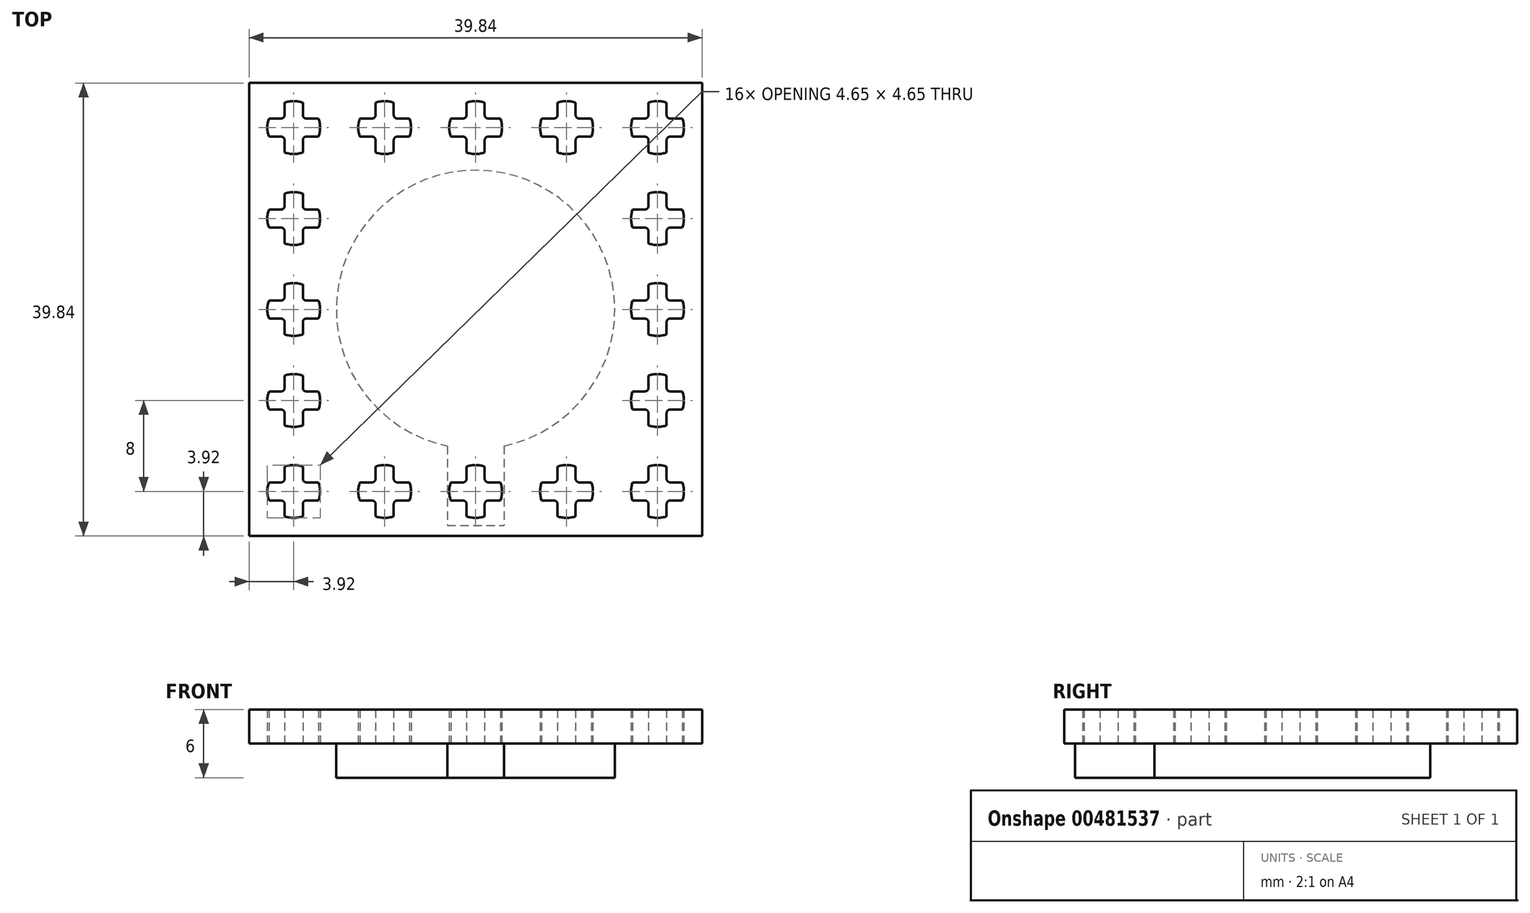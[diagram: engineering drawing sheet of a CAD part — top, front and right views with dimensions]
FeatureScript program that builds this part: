
annotation { "Feature Type Name" : "Feature", "Feature Type Description" : "" }
export const myFeature = defineFeature(function(context is Context, id is Id, definition is map)
    precondition{}
    {
        {
            var Q0;
            Q0=qCreatedBy(makeId("Top.planeOp"),FACE);
            var sketch = newSketch(context, id + "F0", { "sketchPlane" : qUnion([Q0])});
            skLineSegment(sketch, "E0.bottom", {"start": v(-20, 20) * mm, "end": v(20, 20) * mm});
            skLineSegment(sketch, "E0.top", {"start": v(-20, -20) * mm, "end": v(20, -20) * mm});
            skLineSegment(sketch, "E0.left", {"start": v(-20, 20) * mm, "end": v(-20, -20) * mm});
            skLineSegment(sketch, "E0.right", {"start": v(20, 20) * mm, "end": v(20, -20) * mm});
            skLineSegment(sketch, "E1", {"start": v(-16.8, 18.18) * mm, "end": v(-15.2, 18.18) * mm, "construction": true});
            skLineSegment(sketch, "E2", {"start": v(-15.2, 18.18) * mm, "end": v(-15.2, 17.1) * mm});
            skLineSegment(sketch, "E3", {"start": v(-14.9, 16.8) * mm, "end": v(-13.82, 16.8) * mm});
            skLineSegment(sketch, "E4", {"start": v(-13.82, 16.8) * mm, "end": v(-16, 16) * mm, "construction": true});
            skLineSegment(sketch, "E5", {"start": v(-16, 16) * mm, "end": v(-16.8, 18.18) * mm, "construction": true});
            skArc(sketch, "E6", {"start": v(-15.2, 18.18) * mm, "mid": v(-16, 18.32) * mm, "end": v(-16.8, 18.18) * mm});
            skArc(sketch, "E7", {"start": v(-15.2, 17.1) * mm, "mid": v(-15.11, 16.89) * mm, "end": v(-14.9, 16.8) * mm});
            skLineSegment(sketch, "E8", {"start": v(-15.2, 18.18) * mm, "end": v(-15.2, 16.8) * mm, "construction": true});
            skLineSegment(sketch, "E9", {"start": v(-15.2, 16.8) * mm, "end": v(-13.82, 16.8) * mm, "construction": true});
            skArc(sketch, "E10.1.0", {"start": v(-18.18, 16.8) * mm, "mid": v(-18.32, 16) * mm, "end": v(-18.18, 15.2) * mm});
            skArc(sketch, "E10.1.1", {"start": v(-17.1, 16.8) * mm, "mid": v(-16.89, 16.89) * mm, "end": v(-16.8, 17.1) * mm});
            skLineSegment(sketch, "E10.1.2", {"start": v(-18.18, 16.8) * mm, "end": v(-17.1, 16.8) * mm});
            skLineSegment(sketch, "E10.1.3", {"start": v(-16.8, 17.1) * mm, "end": v(-16.8, 18.18) * mm});
            skArc(sketch, "E10.2.0", {"start": v(-16.8, 13.82) * mm, "mid": v(-16, 13.68) * mm, "end": v(-15.2, 13.82) * mm});
            skArc(sketch, "E10.2.1", {"start": v(-16.8, 14.9) * mm, "mid": v(-16.89, 15.11) * mm, "end": v(-17.1, 15.2) * mm});
            skLineSegment(sketch, "E10.2.2", {"start": v(-16.8, 13.82) * mm, "end": v(-16.8, 14.9) * mm});
            skLineSegment(sketch, "E10.2.3", {"start": v(-17.1, 15.2) * mm, "end": v(-18.18, 15.2) * mm});
            skArc(sketch, "E10.3.0", {"start": v(-13.82, 15.2) * mm, "mid": v(-13.67, 16) * mm, "end": v(-13.82, 16.8) * mm});
            skArc(sketch, "E10.3.1", {"start": v(-14.9, 15.2) * mm, "mid": v(-15.11, 15.11) * mm, "end": v(-15.2, 14.9) * mm});
            skLineSegment(sketch, "E10.3.2", {"start": v(-13.82, 15.2) * mm, "end": v(-14.9, 15.2) * mm});
            skLineSegment(sketch, "E10.3.3", {"start": v(-15.2, 14.9) * mm, "end": v(-15.2, 13.82) * mm});
            skArc(sketch, "E11.0.1.0", {"start": v(-15.2, 10.18) * mm, "mid": v(-16, 10.33) * mm, "end": v(-16.8, 10.18) * mm});
            skArc(sketch, "E11.0.1.1", {"start": v(-14.9, 7.2) * mm, "mid": v(-15.11, 7.11) * mm, "end": v(-15.2, 6.9) * mm});
            skLineSegment(sketch, "E11.0.1.2", {"start": v(-13.82, 7.2) * mm, "end": v(-14.9, 7.2) * mm});
            skLineSegment(sketch, "E11.0.1.3", {"start": v(-17.1, 7.2) * mm, "end": v(-18.18, 7.2) * mm});
            skArc(sketch, "E11.0.1.4", {"start": v(-16.8, 6.9) * mm, "mid": v(-16.89, 7.11) * mm, "end": v(-17.1, 7.2) * mm});
            skLineSegment(sketch, "E11.0.1.5", {"start": v(-16.8, 9.1) * mm, "end": v(-16.8, 10.18) * mm});
            skLineSegment(sketch, "E11.0.1.6", {"start": v(-18.18, 8.8) * mm, "end": v(-17.1, 8.8) * mm});
            skArc(sketch, "E11.0.1.7", {"start": v(-17.1, 8.8) * mm, "mid": v(-16.89, 8.89) * mm, "end": v(-16.8, 9.1) * mm});
            skArc(sketch, "E11.0.1.8", {"start": v(-16.8, 5.82) * mm, "mid": v(-16, 5.68) * mm, "end": v(-15.2, 5.82) * mm});
            skArc(sketch, "E11.0.1.9", {"start": v(-18.18, 8.8) * mm, "mid": v(-18.33, 8) * mm, "end": v(-18.18, 7.2) * mm});
            skPoint(sketch, "E11.0.1.10", {"position": v(-16, 8) * mm});
            skLineSegment(sketch, "E11.0.1.11", {"start": v(-16.8, 5.82) * mm, "end": v(-16.8, 6.9) * mm});
            skArc(sketch, "E11.0.1.12", {"start": v(-13.82, 7.2) * mm, "mid": v(-13.68, 8) * mm, "end": v(-13.82, 8.8) * mm});
            skLineSegment(sketch, "E11.0.1.13", {"start": v(-15.2, 6.9) * mm, "end": v(-15.2, 5.82) * mm});
            skLineSegment(sketch, "E11.0.1.14", {"start": v(-15.2, 10.18) * mm, "end": v(-15.2, 9.1) * mm});
            skLineSegment(sketch, "E11.0.1.15", {"start": v(-14.9, 8.8) * mm, "end": v(-13.82, 8.8) * mm});
            skArc(sketch, "E11.0.1.16", {"start": v(-15.2, 9.1) * mm, "mid": v(-15.11, 8.89) * mm, "end": v(-14.9, 8.8) * mm});
            skArc(sketch, "E11.0.2.0", {"start": v(-15.2, 2.18) * mm, "mid": v(-16, 2.33) * mm, "end": v(-16.8, 2.18) * mm});
            skArc(sketch, "E11.0.2.1", {"start": v(-14.9, -0.8) * mm, "mid": v(-15.11, -0.89) * mm, "end": v(-15.2, -1.1) * mm});
            skLineSegment(sketch, "E11.0.2.2", {"start": v(-13.82, -0.8) * mm, "end": v(-14.9, -0.8) * mm});
            skLineSegment(sketch, "E11.0.2.3", {"start": v(-17.1, -0.8) * mm, "end": v(-18.18, -0.8) * mm});
            skArc(sketch, "E11.0.2.4", {"start": v(-16.8, -1.1) * mm, "mid": v(-16.89, -0.89) * mm, "end": v(-17.1, -0.8) * mm});
            skLineSegment(sketch, "E11.0.2.5", {"start": v(-16.8, 1.1) * mm, "end": v(-16.8, 2.18) * mm});
            skLineSegment(sketch, "E11.0.2.6", {"start": v(-18.18, 0.8) * mm, "end": v(-17.1, 0.8) * mm});
            skArc(sketch, "E11.0.2.7", {"start": v(-17.1, 0.8) * mm, "mid": v(-16.89, 0.89) * mm, "end": v(-16.8, 1.1) * mm});
            skArc(sketch, "E11.0.2.8", {"start": v(-16.8, -2.18) * mm, "mid": v(-16, -2.32) * mm, "end": v(-15.2, -2.18) * mm});
            skArc(sketch, "E11.0.2.9", {"start": v(-18.18, 0.8) * mm, "mid": v(-18.33, 0) * mm, "end": v(-18.18, -0.8) * mm});
            skPoint(sketch, "E11.0.2.10", {"position": v(-16, 0) * mm});
            skLineSegment(sketch, "E11.0.2.11", {"start": v(-16.8, -2.18) * mm, "end": v(-16.8, -1.1) * mm});
            skArc(sketch, "E11.0.2.12", {"start": v(-13.82, -0.8) * mm, "mid": v(-13.68, 0) * mm, "end": v(-13.82, 0.8) * mm});
            skLineSegment(sketch, "E11.0.2.13", {"start": v(-15.2, -1.1) * mm, "end": v(-15.2, -2.18) * mm});
            skLineSegment(sketch, "E11.0.2.14", {"start": v(-15.2, 2.18) * mm, "end": v(-15.2, 1.1) * mm});
            skLineSegment(sketch, "E11.0.2.15", {"start": v(-14.9, 0.8) * mm, "end": v(-13.82, 0.8) * mm});
            skArc(sketch, "E11.0.2.16", {"start": v(-15.2, 1.1) * mm, "mid": v(-15.11, 0.89) * mm, "end": v(-14.9, 0.8) * mm});
            skArc(sketch, "E11.0.3.0", {"start": v(-15.2, -5.82) * mm, "mid": v(-16, -5.67) * mm, "end": v(-16.8, -5.82) * mm});
            skArc(sketch, "E11.0.3.1", {"start": v(-14.9, -8.8) * mm, "mid": v(-15.11, -8.89) * mm, "end": v(-15.2, -9.1) * mm});
            skLineSegment(sketch, "E11.0.3.2", {"start": v(-13.82, -8.8) * mm, "end": v(-14.9, -8.8) * mm});
            skLineSegment(sketch, "E11.0.3.3", {"start": v(-17.1, -8.8) * mm, "end": v(-18.18, -8.8) * mm});
            skArc(sketch, "E11.0.3.4", {"start": v(-16.8, -9.1) * mm, "mid": v(-16.89, -8.89) * mm, "end": v(-17.1, -8.8) * mm});
            skLineSegment(sketch, "E11.0.3.5", {"start": v(-16.8, -6.9) * mm, "end": v(-16.8, -5.82) * mm});
            skLineSegment(sketch, "E11.0.3.6", {"start": v(-18.18, -7.2) * mm, "end": v(-17.1, -7.2) * mm});
            skArc(sketch, "E11.0.3.7", {"start": v(-17.1, -7.2) * mm, "mid": v(-16.89, -7.11) * mm, "end": v(-16.8, -6.9) * mm});
            skArc(sketch, "E11.0.3.8", {"start": v(-16.8, -10.18) * mm, "mid": v(-16, -10.32) * mm, "end": v(-15.2, -10.18) * mm});
            skArc(sketch, "E11.0.3.9", {"start": v(-18.18, -7.2) * mm, "mid": v(-18.33, -8) * mm, "end": v(-18.18, -8.8) * mm});
            skPoint(sketch, "E11.0.3.10", {"position": v(-16, -8) * mm});
            skLineSegment(sketch, "E11.0.3.11", {"start": v(-16.8, -10.18) * mm, "end": v(-16.8, -9.1) * mm});
            skArc(sketch, "E11.0.3.12", {"start": v(-13.82, -8.8) * mm, "mid": v(-13.68, -8) * mm, "end": v(-13.82, -7.2) * mm});
            skLineSegment(sketch, "E11.0.3.13", {"start": v(-15.2, -9.1) * mm, "end": v(-15.2, -10.18) * mm});
            skLineSegment(sketch, "E11.0.3.14", {"start": v(-15.2, -5.82) * mm, "end": v(-15.2, -6.9) * mm});
            skLineSegment(sketch, "E11.0.3.15", {"start": v(-14.9, -7.2) * mm, "end": v(-13.82, -7.2) * mm});
            skArc(sketch, "E11.0.3.16", {"start": v(-15.2, -6.9) * mm, "mid": v(-15.11, -7.11) * mm, "end": v(-14.9, -7.2) * mm});
            skArc(sketch, "E11.0.4.0", {"start": v(-15.2, -13.82) * mm, "mid": v(-16, -13.67) * mm, "end": v(-16.8, -13.82) * mm});
            skArc(sketch, "E11.0.4.1", {"start": v(-14.9, -16.8) * mm, "mid": v(-15.11, -16.89) * mm, "end": v(-15.2, -17.1) * mm});
            skLineSegment(sketch, "E11.0.4.2", {"start": v(-13.82, -16.8) * mm, "end": v(-14.9, -16.8) * mm});
            skLineSegment(sketch, "E11.0.4.3", {"start": v(-17.1, -16.8) * mm, "end": v(-18.18, -16.8) * mm});
            skArc(sketch, "E11.0.4.4", {"start": v(-16.8, -17.1) * mm, "mid": v(-16.89, -16.89) * mm, "end": v(-17.1, -16.8) * mm});
            skLineSegment(sketch, "E11.0.4.5", {"start": v(-16.8, -14.9) * mm, "end": v(-16.8, -13.82) * mm});
            skLineSegment(sketch, "E11.0.4.6", {"start": v(-18.18, -15.2) * mm, "end": v(-17.1, -15.2) * mm});
            skArc(sketch, "E11.0.4.7", {"start": v(-17.1, -15.2) * mm, "mid": v(-16.89, -15.11) * mm, "end": v(-16.8, -14.9) * mm});
            skArc(sketch, "E11.0.4.8", {"start": v(-16.8, -18.18) * mm, "mid": v(-16, -18.32) * mm, "end": v(-15.2, -18.18) * mm});
            skArc(sketch, "E11.0.4.9", {"start": v(-18.18, -15.2) * mm, "mid": v(-18.33, -16) * mm, "end": v(-18.18, -16.8) * mm});
            skPoint(sketch, "E11.0.4.10", {"position": v(-16, -16) * mm});
            skLineSegment(sketch, "E11.0.4.11", {"start": v(-16.8, -18.18) * mm, "end": v(-16.8, -17.1) * mm});
            skArc(sketch, "E11.0.4.12", {"start": v(-13.82, -16.8) * mm, "mid": v(-13.68, -16) * mm, "end": v(-13.82, -15.2) * mm});
            skLineSegment(sketch, "E11.0.4.13", {"start": v(-15.2, -17.1) * mm, "end": v(-15.2, -18.18) * mm});
            skLineSegment(sketch, "E11.0.4.14", {"start": v(-15.2, -13.82) * mm, "end": v(-15.2, -14.9) * mm});
            skLineSegment(sketch, "E11.0.4.15", {"start": v(-14.9, -15.2) * mm, "end": v(-13.82, -15.2) * mm});
            skArc(sketch, "E11.0.4.16", {"start": v(-15.2, -14.9) * mm, "mid": v(-15.11, -15.11) * mm, "end": v(-14.9, -15.2) * mm});
            skArc(sketch, "E11.1.0.0", {"start": v(-7.2, 18.18) * mm, "mid": v(-8, 18.32) * mm, "end": v(-8.8, 18.18) * mm});
            skArc(sketch, "E11.1.0.1", {"start": v(-6.9, 15.2) * mm, "mid": v(-7.11, 15.11) * mm, "end": v(-7.2, 14.9) * mm});
            skLineSegment(sketch, "E11.1.0.2", {"start": v(-5.82, 15.2) * mm, "end": v(-6.9, 15.2) * mm});
            skLineSegment(sketch, "E11.1.0.3", {"start": v(-9.1, 15.2) * mm, "end": v(-10.18, 15.2) * mm});
            skArc(sketch, "E11.1.0.4", {"start": v(-8.8, 14.9) * mm, "mid": v(-8.89, 15.11) * mm, "end": v(-9.1, 15.2) * mm});
            skLineSegment(sketch, "E11.1.0.5", {"start": v(-8.8, 17.1) * mm, "end": v(-8.8, 18.18) * mm});
            skLineSegment(sketch, "E11.1.0.6", {"start": v(-10.18, 16.8) * mm, "end": v(-9.1, 16.8) * mm});
            skArc(sketch, "E11.1.0.7", {"start": v(-9.1, 16.8) * mm, "mid": v(-8.89, 16.89) * mm, "end": v(-8.8, 17.1) * mm});
            skArc(sketch, "E11.1.0.8", {"start": v(-8.8, 13.82) * mm, "mid": v(-8, 13.67) * mm, "end": v(-7.2, 13.82) * mm});
            skArc(sketch, "E11.1.0.9", {"start": v(-10.18, 16.8) * mm, "mid": v(-10.33, 16) * mm, "end": v(-10.18, 15.2) * mm});
            skPoint(sketch, "E11.1.0.10", {"position": v(-8, 16) * mm});
            skLineSegment(sketch, "E11.1.0.11", {"start": v(-8.8, 13.82) * mm, "end": v(-8.8, 14.9) * mm});
            skArc(sketch, "E11.1.0.12", {"start": v(-5.82, 15.2) * mm, "mid": v(-5.68, 16) * mm, "end": v(-5.82, 16.8) * mm});
            skLineSegment(sketch, "E11.1.0.13", {"start": v(-7.2, 14.9) * mm, "end": v(-7.2, 13.82) * mm});
            skLineSegment(sketch, "E11.1.0.14", {"start": v(-7.2, 18.18) * mm, "end": v(-7.2, 17.1) * mm});
            skLineSegment(sketch, "E11.1.0.15", {"start": v(-6.9, 16.8) * mm, "end": v(-5.82, 16.8) * mm});
            skArc(sketch, "E11.1.0.16", {"start": v(-7.2, 17.1) * mm, "mid": v(-7.11, 16.89) * mm, "end": v(-6.9, 16.8) * mm});
            skArc(sketch, "E11.1.1.0", {"start": v(-7.2, 10.18) * mm, "mid": v(-8, 10.33) * mm, "end": v(-8.8, 10.18) * mm});
            skArc(sketch, "E11.1.1.1", {"start": v(-6.9, 7.2) * mm, "mid": v(-7.11, 7.11) * mm, "end": v(-7.2, 6.9) * mm});
            skLineSegment(sketch, "E11.1.1.2", {"start": v(-5.82, 7.2) * mm, "end": v(-6.9, 7.2) * mm});
            skLineSegment(sketch, "E11.1.1.3", {"start": v(-9.1, 7.2) * mm, "end": v(-10.18, 7.2) * mm});
            skArc(sketch, "E11.1.1.4", {"start": v(-8.8, 6.9) * mm, "mid": v(-8.89, 7.11) * mm, "end": v(-9.1, 7.2) * mm});
            skLineSegment(sketch, "E11.1.1.5", {"start": v(-8.8, 9.1) * mm, "end": v(-8.8, 10.18) * mm});
            skLineSegment(sketch, "E11.1.1.6", {"start": v(-10.18, 8.8) * mm, "end": v(-9.1, 8.8) * mm});
            skArc(sketch, "E11.1.1.7", {"start": v(-9.1, 8.8) * mm, "mid": v(-8.89, 8.89) * mm, "end": v(-8.8, 9.1) * mm});
            skArc(sketch, "E11.1.1.8", {"start": v(-8.8, 5.82) * mm, "mid": v(-8, 5.68) * mm, "end": v(-7.2, 5.82) * mm});
            skArc(sketch, "E11.1.1.9", {"start": v(-10.18, 8.8) * mm, "mid": v(-10.33, 8) * mm, "end": v(-10.18, 7.2) * mm});
            skPoint(sketch, "E11.1.1.10", {"position": v(-8, 8) * mm});
            skLineSegment(sketch, "E11.1.1.11", {"start": v(-8.8, 5.82) * mm, "end": v(-8.8, 6.9) * mm});
            skArc(sketch, "E11.1.1.12", {"start": v(-5.82, 7.2) * mm, "mid": v(-5.68, 8) * mm, "end": v(-5.82, 8.8) * mm});
            skLineSegment(sketch, "E11.1.1.13", {"start": v(-7.2, 6.9) * mm, "end": v(-7.2, 5.82) * mm});
            skLineSegment(sketch, "E11.1.1.14", {"start": v(-7.2, 10.18) * mm, "end": v(-7.2, 9.1) * mm});
            skLineSegment(sketch, "E11.1.1.15", {"start": v(-6.9, 8.8) * mm, "end": v(-5.82, 8.8) * mm});
            skArc(sketch, "E11.1.1.16", {"start": v(-7.2, 9.1) * mm, "mid": v(-7.11, 8.89) * mm, "end": v(-6.9, 8.8) * mm});
            skArc(sketch, "E11.1.2.0", {"start": v(-7.2, 2.18) * mm, "mid": v(-8, 2.33) * mm, "end": v(-8.8, 2.18) * mm});
            skArc(sketch, "E11.1.2.1", {"start": v(-6.9, -0.8) * mm, "mid": v(-7.11, -0.89) * mm, "end": v(-7.2, -1.1) * mm});
            skLineSegment(sketch, "E11.1.2.2", {"start": v(-5.82, -0.8) * mm, "end": v(-6.9, -0.8) * mm});
            skLineSegment(sketch, "E11.1.2.3", {"start": v(-9.1, -0.8) * mm, "end": v(-10.18, -0.8) * mm});
            skArc(sketch, "E11.1.2.4", {"start": v(-8.8, -1.1) * mm, "mid": v(-8.89, -0.89) * mm, "end": v(-9.1, -0.8) * mm});
            skLineSegment(sketch, "E11.1.2.5", {"start": v(-8.8, 1.1) * mm, "end": v(-8.8, 2.18) * mm});
            skLineSegment(sketch, "E11.1.2.6", {"start": v(-10.18, 0.8) * mm, "end": v(-9.1, 0.8) * mm});
            skArc(sketch, "E11.1.2.7", {"start": v(-9.1, 0.8) * mm, "mid": v(-8.89, 0.89) * mm, "end": v(-8.8, 1.1) * mm});
            skArc(sketch, "E11.1.2.8", {"start": v(-8.8, -2.18) * mm, "mid": v(-8, -2.32) * mm, "end": v(-7.2, -2.18) * mm});
            skArc(sketch, "E11.1.2.9", {"start": v(-10.18, 0.8) * mm, "mid": v(-10.33, 0) * mm, "end": v(-10.18, -0.8) * mm});
            skPoint(sketch, "E11.1.2.10", {"position": v(-8, 0) * mm});
            skLineSegment(sketch, "E11.1.2.11", {"start": v(-8.8, -2.18) * mm, "end": v(-8.8, -1.1) * mm});
            skArc(sketch, "E11.1.2.12", {"start": v(-5.82, -0.8) * mm, "mid": v(-5.68, 0) * mm, "end": v(-5.82, 0.8) * mm});
            skLineSegment(sketch, "E11.1.2.13", {"start": v(-7.2, -1.1) * mm, "end": v(-7.2, -2.18) * mm});
            skLineSegment(sketch, "E11.1.2.14", {"start": v(-7.2, 2.18) * mm, "end": v(-7.2, 1.1) * mm});
            skLineSegment(sketch, "E11.1.2.15", {"start": v(-6.9, 0.8) * mm, "end": v(-5.82, 0.8) * mm});
            skArc(sketch, "E11.1.2.16", {"start": v(-7.2, 1.1) * mm, "mid": v(-7.11, 0.89) * mm, "end": v(-6.9, 0.8) * mm});
            skArc(sketch, "E11.1.3.0", {"start": v(-7.2, -5.82) * mm, "mid": v(-8, -5.67) * mm, "end": v(-8.8, -5.82) * mm});
            skArc(sketch, "E11.1.3.1", {"start": v(-6.9, -8.8) * mm, "mid": v(-7.11, -8.89) * mm, "end": v(-7.2, -9.1) * mm});
            skLineSegment(sketch, "E11.1.3.2", {"start": v(-5.82, -8.8) * mm, "end": v(-6.9, -8.8) * mm});
            skLineSegment(sketch, "E11.1.3.3", {"start": v(-9.1, -8.8) * mm, "end": v(-10.18, -8.8) * mm});
            skArc(sketch, "E11.1.3.4", {"start": v(-8.8, -9.1) * mm, "mid": v(-8.89, -8.89) * mm, "end": v(-9.1, -8.8) * mm});
            skLineSegment(sketch, "E11.1.3.5", {"start": v(-8.8, -6.9) * mm, "end": v(-8.8, -5.82) * mm});
            skLineSegment(sketch, "E11.1.3.6", {"start": v(-10.18, -7.2) * mm, "end": v(-9.1, -7.2) * mm});
            skArc(sketch, "E11.1.3.7", {"start": v(-9.1, -7.2) * mm, "mid": v(-8.89, -7.11) * mm, "end": v(-8.8, -6.9) * mm});
            skArc(sketch, "E11.1.3.8", {"start": v(-8.8, -10.18) * mm, "mid": v(-8, -10.32) * mm, "end": v(-7.2, -10.18) * mm});
            skArc(sketch, "E11.1.3.9", {"start": v(-10.18, -7.2) * mm, "mid": v(-10.33, -8) * mm, "end": v(-10.18, -8.8) * mm});
            skPoint(sketch, "E11.1.3.10", {"position": v(-8, -8) * mm});
            skLineSegment(sketch, "E11.1.3.11", {"start": v(-8.8, -10.18) * mm, "end": v(-8.8, -9.1) * mm});
            skArc(sketch, "E11.1.3.12", {"start": v(-5.82, -8.8) * mm, "mid": v(-5.68, -8) * mm, "end": v(-5.82, -7.2) * mm});
            skLineSegment(sketch, "E11.1.3.13", {"start": v(-7.2, -9.1) * mm, "end": v(-7.2, -10.18) * mm});
            skLineSegment(sketch, "E11.1.3.14", {"start": v(-7.2, -5.82) * mm, "end": v(-7.2, -6.9) * mm});
            skLineSegment(sketch, "E11.1.3.15", {"start": v(-6.9, -7.2) * mm, "end": v(-5.82, -7.2) * mm});
            skArc(sketch, "E11.1.3.16", {"start": v(-7.2, -6.9) * mm, "mid": v(-7.11, -7.11) * mm, "end": v(-6.9, -7.2) * mm});
            skArc(sketch, "E11.1.4.0", {"start": v(-7.2, -13.82) * mm, "mid": v(-8, -13.67) * mm, "end": v(-8.8, -13.82) * mm});
            skArc(sketch, "E11.1.4.1", {"start": v(-6.9, -16.8) * mm, "mid": v(-7.11, -16.89) * mm, "end": v(-7.2, -17.1) * mm});
            skLineSegment(sketch, "E11.1.4.2", {"start": v(-5.82, -16.8) * mm, "end": v(-6.9, -16.8) * mm});
            skLineSegment(sketch, "E11.1.4.3", {"start": v(-9.1, -16.8) * mm, "end": v(-10.18, -16.8) * mm});
            skArc(sketch, "E11.1.4.4", {"start": v(-8.8, -17.1) * mm, "mid": v(-8.89, -16.89) * mm, "end": v(-9.1, -16.8) * mm});
            skLineSegment(sketch, "E11.1.4.5", {"start": v(-8.8, -14.9) * mm, "end": v(-8.8, -13.82) * mm});
            skLineSegment(sketch, "E11.1.4.6", {"start": v(-10.18, -15.2) * mm, "end": v(-9.1, -15.2) * mm});
            skArc(sketch, "E11.1.4.7", {"start": v(-9.1, -15.2) * mm, "mid": v(-8.89, -15.11) * mm, "end": v(-8.8, -14.9) * mm});
            skArc(sketch, "E11.1.4.8", {"start": v(-8.8, -18.18) * mm, "mid": v(-8, -18.32) * mm, "end": v(-7.2, -18.18) * mm});
            skArc(sketch, "E11.1.4.9", {"start": v(-10.18, -15.2) * mm, "mid": v(-10.33, -16) * mm, "end": v(-10.18, -16.8) * mm});
            skPoint(sketch, "E11.1.4.10", {"position": v(-8, -16) * mm});
            skLineSegment(sketch, "E11.1.4.11", {"start": v(-8.8, -18.18) * mm, "end": v(-8.8, -17.1) * mm});
            skArc(sketch, "E11.1.4.12", {"start": v(-5.82, -16.8) * mm, "mid": v(-5.68, -16) * mm, "end": v(-5.82, -15.2) * mm});
            skLineSegment(sketch, "E11.1.4.13", {"start": v(-7.2, -17.1) * mm, "end": v(-7.2, -18.18) * mm});
            skLineSegment(sketch, "E11.1.4.14", {"start": v(-7.2, -13.82) * mm, "end": v(-7.2, -14.9) * mm});
            skLineSegment(sketch, "E11.1.4.15", {"start": v(-6.9, -15.2) * mm, "end": v(-5.82, -15.2) * mm});
            skArc(sketch, "E11.1.4.16", {"start": v(-7.2, -14.9) * mm, "mid": v(-7.11, -15.11) * mm, "end": v(-6.9, -15.2) * mm});
            skArc(sketch, "E11.2.0.0", {"start": v(0.8, 18.18) * mm, "mid": v(0, 18.32) * mm, "end": v(-0.8, 18.18) * mm});
            skArc(sketch, "E11.2.0.1", {"start": v(1.1, 15.2) * mm, "mid": v(0.89, 15.11) * mm, "end": v(0.8, 14.9) * mm});
            skLineSegment(sketch, "E11.2.0.2", {"start": v(2.18, 15.2) * mm, "end": v(1.1, 15.2) * mm});
            skLineSegment(sketch, "E11.2.0.3", {"start": v(-1.1, 15.2) * mm, "end": v(-2.18, 15.2) * mm});
            skArc(sketch, "E11.2.0.4", {"start": v(-0.8, 14.9) * mm, "mid": v(-0.89, 15.11) * mm, "end": v(-1.1, 15.2) * mm});
            skLineSegment(sketch, "E11.2.0.5", {"start": v(-0.8, 17.1) * mm, "end": v(-0.8, 18.18) * mm});
            skLineSegment(sketch, "E11.2.0.6", {"start": v(-2.18, 16.8) * mm, "end": v(-1.1, 16.8) * mm});
            skArc(sketch, "E11.2.0.7", {"start": v(-1.1, 16.8) * mm, "mid": v(-0.89, 16.89) * mm, "end": v(-0.8, 17.1) * mm});
            skArc(sketch, "E11.2.0.8", {"start": v(-0.8, 13.82) * mm, "mid": v(0, 13.68) * mm, "end": v(0.8, 13.82) * mm});
            skArc(sketch, "E11.2.0.9", {"start": v(-2.18, 16.8) * mm, "mid": v(-2.33, 16) * mm, "end": v(-2.18, 15.2) * mm});
            skPoint(sketch, "E11.2.0.10", {"position": v(0, 16) * mm});
            skLineSegment(sketch, "E11.2.0.11", {"start": v(-0.8, 13.82) * mm, "end": v(-0.8, 14.9) * mm});
            skArc(sketch, "E11.2.0.12", {"start": v(2.18, 15.2) * mm, "mid": v(2.32, 16) * mm, "end": v(2.18, 16.8) * mm});
            skLineSegment(sketch, "E11.2.0.13", {"start": v(0.8, 14.9) * mm, "end": v(0.8, 13.82) * mm});
            skLineSegment(sketch, "E11.2.0.14", {"start": v(0.8, 18.18) * mm, "end": v(0.8, 17.1) * mm});
            skLineSegment(sketch, "E11.2.0.15", {"start": v(1.1, 16.8) * mm, "end": v(2.18, 16.8) * mm});
            skArc(sketch, "E11.2.0.16", {"start": v(0.8, 17.1) * mm, "mid": v(0.89, 16.89) * mm, "end": v(1.1, 16.8) * mm});
            skArc(sketch, "E11.2.1.0", {"start": v(0.8, 10.18) * mm, "mid": v(0, 10.33) * mm, "end": v(-0.8, 10.18) * mm});
            skArc(sketch, "E11.2.1.1", {"start": v(1.1, 7.2) * mm, "mid": v(0.89, 7.11) * mm, "end": v(0.8, 6.9) * mm});
            skLineSegment(sketch, "E11.2.1.2", {"start": v(2.18, 7.2) * mm, "end": v(1.1, 7.2) * mm});
            skLineSegment(sketch, "E11.2.1.3", {"start": v(-1.1, 7.2) * mm, "end": v(-2.18, 7.2) * mm});
            skArc(sketch, "E11.2.1.4", {"start": v(-0.8, 6.9) * mm, "mid": v(-0.89, 7.11) * mm, "end": v(-1.1, 7.2) * mm});
            skLineSegment(sketch, "E11.2.1.5", {"start": v(-0.8, 9.1) * mm, "end": v(-0.8, 10.18) * mm});
            skLineSegment(sketch, "E11.2.1.6", {"start": v(-2.18, 8.8) * mm, "end": v(-1.1, 8.8) * mm});
            skArc(sketch, "E11.2.1.7", {"start": v(-1.1, 8.8) * mm, "mid": v(-0.89, 8.89) * mm, "end": v(-0.8, 9.1) * mm});
            skArc(sketch, "E11.2.1.8", {"start": v(-0.8, 5.82) * mm, "mid": v(0, 5.68) * mm, "end": v(0.8, 5.82) * mm});
            skArc(sketch, "E11.2.1.9", {"start": v(-2.18, 8.8) * mm, "mid": v(-2.33, 8) * mm, "end": v(-2.18, 7.2) * mm});
            skPoint(sketch, "E11.2.1.10", {"position": v(0, 8) * mm});
            skLineSegment(sketch, "E11.2.1.11", {"start": v(-0.8, 5.82) * mm, "end": v(-0.8, 6.9) * mm});
            skArc(sketch, "E11.2.1.12", {"start": v(2.18, 7.2) * mm, "mid": v(2.32, 8) * mm, "end": v(2.18, 8.8) * mm});
            skLineSegment(sketch, "E11.2.1.13", {"start": v(0.8, 6.9) * mm, "end": v(0.8, 5.82) * mm});
            skLineSegment(sketch, "E11.2.1.14", {"start": v(0.8, 10.18) * mm, "end": v(0.8, 9.1) * mm});
            skLineSegment(sketch, "E11.2.1.15", {"start": v(1.1, 8.8) * mm, "end": v(2.18, 8.8) * mm});
            skArc(sketch, "E11.2.1.16", {"start": v(0.8, 9.1) * mm, "mid": v(0.89, 8.89) * mm, "end": v(1.1, 8.8) * mm});
            skArc(sketch, "E11.2.2.0", {"start": v(0.8, 2.18) * mm, "mid": v(0, 2.33) * mm, "end": v(-0.8, 2.18) * mm});
            skArc(sketch, "E11.2.2.1", {"start": v(1.1, -0.8) * mm, "mid": v(0.89, -0.89) * mm, "end": v(0.8, -1.1) * mm});
            skLineSegment(sketch, "E11.2.2.2", {"start": v(2.18, -0.8) * mm, "end": v(1.1, -0.8) * mm});
            skLineSegment(sketch, "E11.2.2.3", {"start": v(-1.1, -0.8) * mm, "end": v(-2.18, -0.8) * mm});
            skArc(sketch, "E11.2.2.4", {"start": v(-0.8, -1.1) * mm, "mid": v(-0.89, -0.89) * mm, "end": v(-1.1, -0.8) * mm});
            skLineSegment(sketch, "E11.2.2.5", {"start": v(-0.8, 1.1) * mm, "end": v(-0.8, 2.18) * mm});
            skLineSegment(sketch, "E11.2.2.6", {"start": v(-2.18, 0.8) * mm, "end": v(-1.1, 0.8) * mm});
            skArc(sketch, "E11.2.2.7", {"start": v(-1.1, 0.8) * mm, "mid": v(-0.89, 0.89) * mm, "end": v(-0.8, 1.1) * mm});
            skArc(sketch, "E11.2.2.8", {"start": v(-0.8, -2.18) * mm, "mid": v(0, -2.32) * mm, "end": v(0.8, -2.18) * mm});
            skArc(sketch, "E11.2.2.9", {"start": v(-2.18, 0.8) * mm, "mid": v(-2.33, 0) * mm, "end": v(-2.18, -0.8) * mm});
            skPoint(sketch, "E11.2.2.10", {"position": v(0, 0) * mm});
            skLineSegment(sketch, "E11.2.2.11", {"start": v(-0.8, -2.18) * mm, "end": v(-0.8, -1.1) * mm});
            skArc(sketch, "E11.2.2.12", {"start": v(2.18, -0.8) * mm, "mid": v(2.32, 0) * mm, "end": v(2.18, 0.8) * mm});
            skLineSegment(sketch, "E11.2.2.13", {"start": v(0.8, -1.1) * mm, "end": v(0.8, -2.18) * mm});
            skLineSegment(sketch, "E11.2.2.14", {"start": v(0.8, 2.18) * mm, "end": v(0.8, 1.1) * mm});
            skLineSegment(sketch, "E11.2.2.15", {"start": v(1.1, 0.8) * mm, "end": v(2.18, 0.8) * mm});
            skArc(sketch, "E11.2.2.16", {"start": v(0.8, 1.1) * mm, "mid": v(0.89, 0.89) * mm, "end": v(1.1, 0.8) * mm});
            skArc(sketch, "E11.2.3.0", {"start": v(0.8, -5.82) * mm, "mid": v(0, -5.67) * mm, "end": v(-0.8, -5.82) * mm});
            skArc(sketch, "E11.2.3.1", {"start": v(1.1, -8.8) * mm, "mid": v(0.89, -8.89) * mm, "end": v(0.8, -9.1) * mm});
            skLineSegment(sketch, "E11.2.3.2", {"start": v(2.18, -8.8) * mm, "end": v(1.1, -8.8) * mm});
            skLineSegment(sketch, "E11.2.3.3", {"start": v(-1.1, -8.8) * mm, "end": v(-2.18, -8.8) * mm});
            skArc(sketch, "E11.2.3.4", {"start": v(-0.8, -9.1) * mm, "mid": v(-0.89, -8.89) * mm, "end": v(-1.1, -8.8) * mm});
            skLineSegment(sketch, "E11.2.3.5", {"start": v(-0.8, -6.9) * mm, "end": v(-0.8, -5.82) * mm});
            skLineSegment(sketch, "E11.2.3.6", {"start": v(-2.18, -7.2) * mm, "end": v(-1.1, -7.2) * mm});
            skArc(sketch, "E11.2.3.7", {"start": v(-1.1, -7.2) * mm, "mid": v(-0.89, -7.11) * mm, "end": v(-0.8, -6.9) * mm});
            skArc(sketch, "E11.2.3.8", {"start": v(-0.8, -10.18) * mm, "mid": v(0, -10.32) * mm, "end": v(0.8, -10.18) * mm});
            skArc(sketch, "E11.2.3.9", {"start": v(-2.18, -7.2) * mm, "mid": v(-2.33, -8) * mm, "end": v(-2.18, -8.8) * mm});
            skPoint(sketch, "E11.2.3.10", {"position": v(0, -8) * mm});
            skLineSegment(sketch, "E11.2.3.11", {"start": v(-0.8, -10.18) * mm, "end": v(-0.8, -9.1) * mm});
            skArc(sketch, "E11.2.3.12", {"start": v(2.18, -8.8) * mm, "mid": v(2.32, -8) * mm, "end": v(2.18, -7.2) * mm});
            skLineSegment(sketch, "E11.2.3.13", {"start": v(0.8, -9.1) * mm, "end": v(0.8, -10.18) * mm});
            skLineSegment(sketch, "E11.2.3.14", {"start": v(0.8, -5.82) * mm, "end": v(0.8, -6.9) * mm});
            skLineSegment(sketch, "E11.2.3.15", {"start": v(1.1, -7.2) * mm, "end": v(2.18, -7.2) * mm});
            skArc(sketch, "E11.2.3.16", {"start": v(0.8, -6.9) * mm, "mid": v(0.89, -7.11) * mm, "end": v(1.1, -7.2) * mm});
            skArc(sketch, "E11.2.4.0", {"start": v(0.8, -13.82) * mm, "mid": v(0, -13.67) * mm, "end": v(-0.8, -13.82) * mm});
            skArc(sketch, "E11.2.4.1", {"start": v(1.1, -16.8) * mm, "mid": v(0.89, -16.89) * mm, "end": v(0.8, -17.1) * mm});
            skLineSegment(sketch, "E11.2.4.2", {"start": v(2.18, -16.8) * mm, "end": v(1.1, -16.8) * mm});
            skLineSegment(sketch, "E11.2.4.3", {"start": v(-1.1, -16.8) * mm, "end": v(-2.18, -16.8) * mm});
            skArc(sketch, "E11.2.4.4", {"start": v(-0.8, -17.1) * mm, "mid": v(-0.89, -16.89) * mm, "end": v(-1.1, -16.8) * mm});
            skLineSegment(sketch, "E11.2.4.5", {"start": v(-0.8, -14.9) * mm, "end": v(-0.8, -13.82) * mm});
            skLineSegment(sketch, "E11.2.4.6", {"start": v(-2.18, -15.2) * mm, "end": v(-1.1, -15.2) * mm});
            skArc(sketch, "E11.2.4.7", {"start": v(-1.1, -15.2) * mm, "mid": v(-0.89, -15.11) * mm, "end": v(-0.8, -14.9) * mm});
            skArc(sketch, "E11.2.4.8", {"start": v(-0.8, -18.18) * mm, "mid": v(0, -18.32) * mm, "end": v(0.8, -18.18) * mm});
            skArc(sketch, "E11.2.4.9", {"start": v(-2.18, -15.2) * mm, "mid": v(-2.33, -16) * mm, "end": v(-2.18, -16.8) * mm});
            skPoint(sketch, "E11.2.4.10", {"position": v(0, -16) * mm});
            skLineSegment(sketch, "E11.2.4.11", {"start": v(-0.8, -18.18) * mm, "end": v(-0.8, -17.1) * mm});
            skArc(sketch, "E11.2.4.12", {"start": v(2.18, -16.8) * mm, "mid": v(2.32, -16) * mm, "end": v(2.18, -15.2) * mm});
            skLineSegment(sketch, "E11.2.4.13", {"start": v(0.8, -17.1) * mm, "end": v(0.8, -18.18) * mm});
            skLineSegment(sketch, "E11.2.4.14", {"start": v(0.8, -13.82) * mm, "end": v(0.8, -14.9) * mm});
            skLineSegment(sketch, "E11.2.4.15", {"start": v(1.1, -15.2) * mm, "end": v(2.18, -15.2) * mm});
            skArc(sketch, "E11.2.4.16", {"start": v(0.8, -14.9) * mm, "mid": v(0.89, -15.11) * mm, "end": v(1.1, -15.2) * mm});
            skLineSegment(sketch, "E11.direction1", {"start": v(-16.8, 13.82) * mm, "end": v(-8.8, 13.82) * mm, "construction": true});
            skLineSegment(sketch, "E11.direction2", {"start": v(-16.8, 13.82) * mm, "end": v(-16.8, 5.82) * mm, "construction": true});
            skLineSegment(sketch, "E12.bottom", {"start": v(-19.93, 19.93) * mm, "end": v(19.92, 19.92) * mm});
            skLineSegment(sketch, "E12.top", {"start": v(-19.93, -19.92) * mm, "end": v(19.92, -19.93) * mm});
            skLineSegment(sketch, "E12.left", {"start": v(-19.93, 19.93) * mm, "end": v(-19.93, -19.92) * mm});
            skLineSegment(sketch, "E12.right", {"start": v(19.93, 19.92) * mm, "end": v(19.92, -19.93) * mm});
            skArc(sketch, "E13.0.3.0", {"start": v(8.8, 18.18) * mm, "mid": v(8, 18.32) * mm, "end": v(7.2, 18.18) * mm});
            skArc(sketch, "E13.4.3.0", {"start": v(9.1, 15.2) * mm, "mid": v(8.89, 15.11) * mm, "end": v(8.8, 14.9) * mm});
            skLineSegment(sketch, "E13.8.3.0", {"start": v(10.18, 15.2) * mm, "end": v(9.1, 15.2) * mm});
            skLineSegment(sketch, "E13.11.3.0", {"start": v(6.9, 15.2) * mm, "end": v(5.82, 15.2) * mm});
            skArc(sketch, "E13.14.3.0", {"start": v(7.2, 14.9) * mm, "mid": v(7.11, 15.11) * mm, "end": v(6.9, 15.2) * mm});
            skLineSegment(sketch, "E13.18.3.0", {"start": v(7.2, 17.1) * mm, "end": v(7.2, 18.18) * mm});
            skLineSegment(sketch, "E13.21.3.0", {"start": v(5.82, 16.8) * mm, "end": v(6.9, 16.8) * mm});
            skArc(sketch, "E13.24.3.0", {"start": v(6.9, 16.8) * mm, "mid": v(7.11, 16.89) * mm, "end": v(7.2, 17.1) * mm});
            skArc(sketch, "E13.28.3.0", {"start": v(7.2, 13.82) * mm, "mid": v(8, 13.67) * mm, "end": v(8.8, 13.82) * mm});
            skArc(sketch, "E13.32.3.0", {"start": v(5.82, 16.8) * mm, "mid": v(5.67, 16) * mm, "end": v(5.82, 15.2) * mm});
            skPoint(sketch, "E13.36.3.0", {"position": v(8, 16) * mm});
            skLineSegment(sketch, "E13.37.3.0", {"start": v(7.2, 13.82) * mm, "end": v(7.2, 14.9) * mm});
            skArc(sketch, "E13.40.3.0", {"start": v(10.18, 15.2) * mm, "mid": v(10.32, 16) * mm, "end": v(10.18, 16.8) * mm});
            skLineSegment(sketch, "E13.44.3.0", {"start": v(8.8, 14.9) * mm, "end": v(8.8, 13.82) * mm});
            skLineSegment(sketch, "E13.47.3.0", {"start": v(8.8, 18.18) * mm, "end": v(8.8, 17.1) * mm});
            skLineSegment(sketch, "E13.50.3.0", {"start": v(9.1, 16.8) * mm, "end": v(10.18, 16.8) * mm});
            skArc(sketch, "E13.53.3.0", {"start": v(8.8, 17.1) * mm, "mid": v(8.89, 16.89) * mm, "end": v(9.1, 16.8) * mm});
            skArc(sketch, "E13.0.3.1", {"start": v(8.8, 10.18) * mm, "mid": v(8, 10.33) * mm, "end": v(7.2, 10.18) * mm});
            skArc(sketch, "E13.4.3.1", {"start": v(9.1, 7.2) * mm, "mid": v(8.89, 7.11) * mm, "end": v(8.8, 6.9) * mm});
            skLineSegment(sketch, "E13.8.3.1", {"start": v(10.18, 7.2) * mm, "end": v(9.1, 7.2) * mm});
            skLineSegment(sketch, "E13.11.3.1", {"start": v(6.9, 7.2) * mm, "end": v(5.82, 7.2) * mm});
            skArc(sketch, "E13.14.3.1", {"start": v(7.2, 6.9) * mm, "mid": v(7.11, 7.11) * mm, "end": v(6.9, 7.2) * mm});
            skLineSegment(sketch, "E13.18.3.1", {"start": v(7.2, 9.1) * mm, "end": v(7.2, 10.18) * mm});
            skLineSegment(sketch, "E13.21.3.1", {"start": v(5.82, 8.8) * mm, "end": v(6.9, 8.8) * mm});
            skArc(sketch, "E13.24.3.1", {"start": v(6.9, 8.8) * mm, "mid": v(7.11, 8.89) * mm, "end": v(7.2, 9.1) * mm});
            skArc(sketch, "E13.28.3.1", {"start": v(7.2, 5.82) * mm, "mid": v(8, 5.68) * mm, "end": v(8.8, 5.82) * mm});
            skArc(sketch, "E13.32.3.1", {"start": v(5.82, 8.8) * mm, "mid": v(5.67, 8) * mm, "end": v(5.82, 7.2) * mm});
            skPoint(sketch, "E13.36.3.1", {"position": v(8, 8) * mm});
            skLineSegment(sketch, "E13.37.3.1", {"start": v(7.2, 5.82) * mm, "end": v(7.2, 6.9) * mm});
            skArc(sketch, "E13.40.3.1", {"start": v(10.18, 7.2) * mm, "mid": v(10.32, 8) * mm, "end": v(10.18, 8.8) * mm});
            skLineSegment(sketch, "E13.44.3.1", {"start": v(8.8, 6.9) * mm, "end": v(8.8, 5.82) * mm});
            skLineSegment(sketch, "E13.47.3.1", {"start": v(8.8, 10.18) * mm, "end": v(8.8, 9.1) * mm});
            skLineSegment(sketch, "E13.50.3.1", {"start": v(9.1, 8.8) * mm, "end": v(10.18, 8.8) * mm});
            skArc(sketch, "E13.53.3.1", {"start": v(8.8, 9.1) * mm, "mid": v(8.89, 8.89) * mm, "end": v(9.1, 8.8) * mm});
            skArc(sketch, "E13.0.3.2", {"start": v(8.8, 2.18) * mm, "mid": v(8, 2.33) * mm, "end": v(7.2, 2.18) * mm});
            skArc(sketch, "E13.4.3.2", {"start": v(9.1, -0.8) * mm, "mid": v(8.89, -0.89) * mm, "end": v(8.8, -1.1) * mm});
            skLineSegment(sketch, "E13.8.3.2", {"start": v(10.18, -0.8) * mm, "end": v(9.1, -0.8) * mm});
            skLineSegment(sketch, "E13.11.3.2", {"start": v(6.9, -0.8) * mm, "end": v(5.82, -0.8) * mm});
            skArc(sketch, "E13.14.3.2", {"start": v(7.2, -1.1) * mm, "mid": v(7.11, -0.89) * mm, "end": v(6.9, -0.8) * mm});
            skLineSegment(sketch, "E13.18.3.2", {"start": v(7.2, 1.1) * mm, "end": v(7.2, 2.18) * mm});
            skLineSegment(sketch, "E13.21.3.2", {"start": v(5.82, 0.8) * mm, "end": v(6.9, 0.8) * mm});
            skArc(sketch, "E13.24.3.2", {"start": v(6.9, 0.8) * mm, "mid": v(7.11, 0.89) * mm, "end": v(7.2, 1.1) * mm});
            skArc(sketch, "E13.28.3.2", {"start": v(7.2, -2.18) * mm, "mid": v(8, -2.32) * mm, "end": v(8.8, -2.18) * mm});
            skArc(sketch, "E13.32.3.2", {"start": v(5.82, 0.8) * mm, "mid": v(5.67, 0) * mm, "end": v(5.82, -0.8) * mm});
            skPoint(sketch, "E13.36.3.2", {"position": v(8, 0) * mm});
            skLineSegment(sketch, "E13.37.3.2", {"start": v(7.2, -2.18) * mm, "end": v(7.2, -1.1) * mm});
            skArc(sketch, "E13.40.3.2", {"start": v(10.18, -0.8) * mm, "mid": v(10.32, 0) * mm, "end": v(10.18, 0.8) * mm});
            skLineSegment(sketch, "E13.44.3.2", {"start": v(8.8, -1.1) * mm, "end": v(8.8, -2.18) * mm});
            skLineSegment(sketch, "E13.47.3.2", {"start": v(8.8, 2.18) * mm, "end": v(8.8, 1.1) * mm});
            skLineSegment(sketch, "E13.50.3.2", {"start": v(9.1, 0.8) * mm, "end": v(10.18, 0.8) * mm});
            skArc(sketch, "E13.53.3.2", {"start": v(8.8, 1.1) * mm, "mid": v(8.89, 0.89) * mm, "end": v(9.1, 0.8) * mm});
            skArc(sketch, "E13.0.3.3", {"start": v(8.8, -5.82) * mm, "mid": v(8, -5.67) * mm, "end": v(7.2, -5.82) * mm});
            skArc(sketch, "E13.4.3.3", {"start": v(9.1, -8.8) * mm, "mid": v(8.89, -8.89) * mm, "end": v(8.8, -9.1) * mm});
            skLineSegment(sketch, "E13.8.3.3", {"start": v(10.18, -8.8) * mm, "end": v(9.1, -8.8) * mm});
            skLineSegment(sketch, "E13.11.3.3", {"start": v(6.9, -8.8) * mm, "end": v(5.82, -8.8) * mm});
            skArc(sketch, "E13.14.3.3", {"start": v(7.2, -9.1) * mm, "mid": v(7.11, -8.89) * mm, "end": v(6.9, -8.8) * mm});
            skLineSegment(sketch, "E13.18.3.3", {"start": v(7.2, -6.9) * mm, "end": v(7.2, -5.82) * mm});
            skLineSegment(sketch, "E13.21.3.3", {"start": v(5.82, -7.2) * mm, "end": v(6.9, -7.2) * mm});
            skArc(sketch, "E13.24.3.3", {"start": v(6.9, -7.2) * mm, "mid": v(7.11, -7.11) * mm, "end": v(7.2, -6.9) * mm});
            skArc(sketch, "E13.28.3.3", {"start": v(7.2, -10.18) * mm, "mid": v(8, -10.32) * mm, "end": v(8.8, -10.18) * mm});
            skArc(sketch, "E13.32.3.3", {"start": v(5.82, -7.2) * mm, "mid": v(5.67, -8) * mm, "end": v(5.82, -8.8) * mm});
            skPoint(sketch, "E13.36.3.3", {"position": v(8, -8) * mm});
            skLineSegment(sketch, "E13.37.3.3", {"start": v(7.2, -10.18) * mm, "end": v(7.2, -9.1) * mm});
            skArc(sketch, "E13.40.3.3", {"start": v(10.18, -8.8) * mm, "mid": v(10.32, -8) * mm, "end": v(10.18, -7.2) * mm});
            skLineSegment(sketch, "E13.44.3.3", {"start": v(8.8, -9.1) * mm, "end": v(8.8, -10.18) * mm});
            skLineSegment(sketch, "E13.47.3.3", {"start": v(8.8, -5.82) * mm, "end": v(8.8, -6.9) * mm});
            skLineSegment(sketch, "E13.50.3.3", {"start": v(9.1, -7.2) * mm, "end": v(10.18, -7.2) * mm});
            skArc(sketch, "E13.53.3.3", {"start": v(8.8, -6.9) * mm, "mid": v(8.89, -7.11) * mm, "end": v(9.1, -7.2) * mm});
            skArc(sketch, "E13.0.3.4", {"start": v(8.8, -13.82) * mm, "mid": v(8, -13.67) * mm, "end": v(7.2, -13.82) * mm});
            skArc(sketch, "E13.4.3.4", {"start": v(9.1, -16.8) * mm, "mid": v(8.89, -16.89) * mm, "end": v(8.8, -17.1) * mm});
            skLineSegment(sketch, "E13.8.3.4", {"start": v(10.18, -16.8) * mm, "end": v(9.1, -16.8) * mm});
            skLineSegment(sketch, "E13.11.3.4", {"start": v(6.9, -16.8) * mm, "end": v(5.82, -16.8) * mm});
            skArc(sketch, "E13.14.3.4", {"start": v(7.2, -17.1) * mm, "mid": v(7.11, -16.89) * mm, "end": v(6.9, -16.8) * mm});
            skLineSegment(sketch, "E13.18.3.4", {"start": v(7.2, -14.9) * mm, "end": v(7.2, -13.82) * mm});
            skLineSegment(sketch, "E13.21.3.4", {"start": v(5.82, -15.2) * mm, "end": v(6.9, -15.2) * mm});
            skArc(sketch, "E13.24.3.4", {"start": v(6.9, -15.2) * mm, "mid": v(7.11, -15.11) * mm, "end": v(7.2, -14.9) * mm});
            skArc(sketch, "E13.28.3.4", {"start": v(7.2, -18.18) * mm, "mid": v(8, -18.32) * mm, "end": v(8.8, -18.18) * mm});
            skArc(sketch, "E13.32.3.4", {"start": v(5.82, -15.2) * mm, "mid": v(5.67, -16) * mm, "end": v(5.82, -16.8) * mm});
            skPoint(sketch, "E13.36.3.4", {"position": v(8, -16) * mm});
            skLineSegment(sketch, "E13.37.3.4", {"start": v(7.2, -18.18) * mm, "end": v(7.2, -17.1) * mm});
            skArc(sketch, "E13.40.3.4", {"start": v(10.18, -16.8) * mm, "mid": v(10.32, -16) * mm, "end": v(10.18, -15.2) * mm});
            skLineSegment(sketch, "E13.44.3.4", {"start": v(8.8, -17.1) * mm, "end": v(8.8, -18.18) * mm});
            skLineSegment(sketch, "E13.47.3.4", {"start": v(8.8, -13.82) * mm, "end": v(8.8, -14.9) * mm});
            skLineSegment(sketch, "E13.50.3.4", {"start": v(9.1, -15.2) * mm, "end": v(10.18, -15.2) * mm});
            skArc(sketch, "E13.53.3.4", {"start": v(8.8, -14.9) * mm, "mid": v(8.89, -15.11) * mm, "end": v(9.1, -15.2) * mm});
            skArc(sketch, "E14.0.4.0", {"start": v(16.8, 18.18) * mm, "mid": v(16, 18.32) * mm, "end": v(15.2, 18.18) * mm});
            skArc(sketch, "E14.4.4.0", {"start": v(17.1, 15.2) * mm, "mid": v(16.89, 15.11) * mm, "end": v(16.8, 14.9) * mm});
            skLineSegment(sketch, "E14.8.4.0", {"start": v(18.18, 15.2) * mm, "end": v(17.1, 15.2) * mm});
            skLineSegment(sketch, "E14.11.4.0", {"start": v(14.9, 15.2) * mm, "end": v(13.82, 15.2) * mm});
            skArc(sketch, "E14.14.4.0", {"start": v(15.2, 14.9) * mm, "mid": v(15.11, 15.11) * mm, "end": v(14.9, 15.2) * mm});
            skLineSegment(sketch, "E14.18.4.0", {"start": v(15.2, 17.1) * mm, "end": v(15.2, 18.18) * mm});
            skLineSegment(sketch, "E14.21.4.0", {"start": v(13.82, 16.8) * mm, "end": v(14.9, 16.8) * mm});
            skArc(sketch, "E14.24.4.0", {"start": v(14.9, 16.8) * mm, "mid": v(15.11, 16.89) * mm, "end": v(15.2, 17.1) * mm});
            skArc(sketch, "E14.28.4.0", {"start": v(15.2, 13.82) * mm, "mid": v(16, 13.67) * mm, "end": v(16.8, 13.82) * mm});
            skArc(sketch, "E14.32.4.0", {"start": v(13.82, 16.8) * mm, "mid": v(13.67, 16) * mm, "end": v(13.82, 15.2) * mm});
            skPoint(sketch, "E14.36.4.0", {"position": v(16, 16) * mm});
            skLineSegment(sketch, "E14.37.4.0", {"start": v(15.2, 13.82) * mm, "end": v(15.2, 14.9) * mm});
            skArc(sketch, "E14.40.4.0", {"start": v(18.18, 15.2) * mm, "mid": v(18.32, 16) * mm, "end": v(18.18, 16.8) * mm});
            skLineSegment(sketch, "E14.44.4.0", {"start": v(16.8, 14.9) * mm, "end": v(16.8, 13.82) * mm});
            skLineSegment(sketch, "E14.47.4.0", {"start": v(16.8, 18.18) * mm, "end": v(16.8, 17.1) * mm});
            skLineSegment(sketch, "E14.50.4.0", {"start": v(17.1, 16.8) * mm, "end": v(18.18, 16.8) * mm});
            skArc(sketch, "E14.53.4.0", {"start": v(16.8, 17.1) * mm, "mid": v(16.89, 16.89) * mm, "end": v(17.1, 16.8) * mm});
            skArc(sketch, "E14.0.4.1", {"start": v(16.8, 10.18) * mm, "mid": v(16, 10.33) * mm, "end": v(15.2, 10.18) * mm});
            skArc(sketch, "E14.4.4.1", {"start": v(17.1, 7.2) * mm, "mid": v(16.89, 7.11) * mm, "end": v(16.8, 6.9) * mm});
            skLineSegment(sketch, "E14.8.4.1", {"start": v(18.18, 7.2) * mm, "end": v(17.1, 7.2) * mm});
            skLineSegment(sketch, "E14.11.4.1", {"start": v(14.9, 7.2) * mm, "end": v(13.82, 7.2) * mm});
            skArc(sketch, "E14.14.4.1", {"start": v(15.2, 6.9) * mm, "mid": v(15.11, 7.11) * mm, "end": v(14.9, 7.2) * mm});
            skLineSegment(sketch, "E14.18.4.1", {"start": v(15.2, 9.1) * mm, "end": v(15.2, 10.18) * mm});
            skLineSegment(sketch, "E14.21.4.1", {"start": v(13.82, 8.8) * mm, "end": v(14.9, 8.8) * mm});
            skArc(sketch, "E14.24.4.1", {"start": v(14.9, 8.8) * mm, "mid": v(15.11, 8.89) * mm, "end": v(15.2, 9.1) * mm});
            skArc(sketch, "E14.28.4.1", {"start": v(15.2, 5.82) * mm, "mid": v(16, 5.68) * mm, "end": v(16.8, 5.82) * mm});
            skArc(sketch, "E14.32.4.1", {"start": v(13.82, 8.8) * mm, "mid": v(13.67, 8) * mm, "end": v(13.82, 7.2) * mm});
            skPoint(sketch, "E14.36.4.1", {"position": v(16, 8) * mm});
            skLineSegment(sketch, "E14.37.4.1", {"start": v(15.2, 5.82) * mm, "end": v(15.2, 6.9) * mm});
            skArc(sketch, "E14.40.4.1", {"start": v(18.18, 7.2) * mm, "mid": v(18.32, 8) * mm, "end": v(18.18, 8.8) * mm});
            skLineSegment(sketch, "E14.44.4.1", {"start": v(16.8, 6.9) * mm, "end": v(16.8, 5.82) * mm});
            skLineSegment(sketch, "E14.47.4.1", {"start": v(16.8, 10.18) * mm, "end": v(16.8, 9.1) * mm});
            skLineSegment(sketch, "E14.50.4.1", {"start": v(17.1, 8.8) * mm, "end": v(18.18, 8.8) * mm});
            skArc(sketch, "E14.53.4.1", {"start": v(16.8, 9.1) * mm, "mid": v(16.89, 8.89) * mm, "end": v(17.1, 8.8) * mm});
            skArc(sketch, "E14.0.4.2", {"start": v(16.8, 2.18) * mm, "mid": v(16, 2.33) * mm, "end": v(15.2, 2.18) * mm});
            skArc(sketch, "E14.4.4.2", {"start": v(17.1, -0.8) * mm, "mid": v(16.89, -0.89) * mm, "end": v(16.8, -1.1) * mm});
            skLineSegment(sketch, "E14.8.4.2", {"start": v(18.18, -0.8) * mm, "end": v(17.1, -0.8) * mm});
            skLineSegment(sketch, "E14.11.4.2", {"start": v(14.9, -0.8) * mm, "end": v(13.82, -0.8) * mm});
            skArc(sketch, "E14.14.4.2", {"start": v(15.2, -1.1) * mm, "mid": v(15.11, -0.89) * mm, "end": v(14.9, -0.8) * mm});
            skLineSegment(sketch, "E14.18.4.2", {"start": v(15.2, 1.1) * mm, "end": v(15.2, 2.18) * mm});
            skLineSegment(sketch, "E14.21.4.2", {"start": v(13.82, 0.8) * mm, "end": v(14.9, 0.8) * mm});
            skArc(sketch, "E14.24.4.2", {"start": v(14.9, 0.8) * mm, "mid": v(15.11, 0.89) * mm, "end": v(15.2, 1.1) * mm});
            skArc(sketch, "E14.28.4.2", {"start": v(15.2, -2.18) * mm, "mid": v(16, -2.32) * mm, "end": v(16.8, -2.18) * mm});
            skArc(sketch, "E14.32.4.2", {"start": v(13.82, 0.8) * mm, "mid": v(13.67, 0) * mm, "end": v(13.82, -0.8) * mm});
            skPoint(sketch, "E14.36.4.2", {"position": v(16, 0) * mm});
            skLineSegment(sketch, "E14.37.4.2", {"start": v(15.2, -2.18) * mm, "end": v(15.2, -1.1) * mm});
            skArc(sketch, "E14.40.4.2", {"start": v(18.18, -0.8) * mm, "mid": v(18.32, 0) * mm, "end": v(18.18, 0.8) * mm});
            skLineSegment(sketch, "E14.44.4.2", {"start": v(16.8, -1.1) * mm, "end": v(16.8, -2.18) * mm});
            skLineSegment(sketch, "E14.47.4.2", {"start": v(16.8, 2.18) * mm, "end": v(16.8, 1.1) * mm});
            skLineSegment(sketch, "E14.50.4.2", {"start": v(17.1, 0.8) * mm, "end": v(18.18, 0.8) * mm});
            skArc(sketch, "E14.53.4.2", {"start": v(16.8, 1.1) * mm, "mid": v(16.89, 0.89) * mm, "end": v(17.1, 0.8) * mm});
            skArc(sketch, "E14.0.4.3", {"start": v(16.8, -5.82) * mm, "mid": v(16, -5.67) * mm, "end": v(15.2, -5.82) * mm});
            skArc(sketch, "E14.4.4.3", {"start": v(17.1, -8.8) * mm, "mid": v(16.89, -8.89) * mm, "end": v(16.8, -9.1) * mm});
            skLineSegment(sketch, "E14.8.4.3", {"start": v(18.18, -8.8) * mm, "end": v(17.1, -8.8) * mm});
            skLineSegment(sketch, "E14.11.4.3", {"start": v(14.9, -8.8) * mm, "end": v(13.82, -8.8) * mm});
            skArc(sketch, "E14.14.4.3", {"start": v(15.2, -9.1) * mm, "mid": v(15.11, -8.89) * mm, "end": v(14.9, -8.8) * mm});
            skLineSegment(sketch, "E14.18.4.3", {"start": v(15.2, -6.9) * mm, "end": v(15.2, -5.82) * mm});
            skLineSegment(sketch, "E14.21.4.3", {"start": v(13.82, -7.2) * mm, "end": v(14.9, -7.2) * mm});
            skArc(sketch, "E14.24.4.3", {"start": v(14.9, -7.2) * mm, "mid": v(15.11, -7.11) * mm, "end": v(15.2, -6.9) * mm});
            skArc(sketch, "E14.28.4.3", {"start": v(15.2, -10.18) * mm, "mid": v(16, -10.32) * mm, "end": v(16.8, -10.18) * mm});
            skArc(sketch, "E14.32.4.3", {"start": v(13.82, -7.2) * mm, "mid": v(13.67, -8) * mm, "end": v(13.82, -8.8) * mm});
            skPoint(sketch, "E14.36.4.3", {"position": v(16, -8) * mm});
            skLineSegment(sketch, "E14.37.4.3", {"start": v(15.2, -10.18) * mm, "end": v(15.2, -9.1) * mm});
            skArc(sketch, "E14.40.4.3", {"start": v(18.18, -8.8) * mm, "mid": v(18.32, -8) * mm, "end": v(18.18, -7.2) * mm});
            skLineSegment(sketch, "E14.44.4.3", {"start": v(16.8, -9.1) * mm, "end": v(16.8, -10.18) * mm});
            skLineSegment(sketch, "E14.47.4.3", {"start": v(16.8, -5.82) * mm, "end": v(16.8, -6.9) * mm});
            skLineSegment(sketch, "E14.50.4.3", {"start": v(17.1, -7.2) * mm, "end": v(18.18, -7.2) * mm});
            skArc(sketch, "E14.53.4.3", {"start": v(16.8, -6.9) * mm, "mid": v(16.89, -7.11) * mm, "end": v(17.1, -7.2) * mm});
            skArc(sketch, "E14.0.4.4", {"start": v(16.8, -13.82) * mm, "mid": v(16, -13.67) * mm, "end": v(15.2, -13.82) * mm});
            skArc(sketch, "E14.4.4.4", {"start": v(17.1, -16.8) * mm, "mid": v(16.89, -16.89) * mm, "end": v(16.8, -17.1) * mm});
            skLineSegment(sketch, "E14.8.4.4", {"start": v(18.18, -16.8) * mm, "end": v(17.1, -16.8) * mm});
            skLineSegment(sketch, "E14.11.4.4", {"start": v(14.9, -16.8) * mm, "end": v(13.82, -16.8) * mm});
            skArc(sketch, "E14.14.4.4", {"start": v(15.2, -17.1) * mm, "mid": v(15.11, -16.89) * mm, "end": v(14.9, -16.8) * mm});
            skLineSegment(sketch, "E14.18.4.4", {"start": v(15.2, -14.9) * mm, "end": v(15.2, -13.82) * mm});
            skLineSegment(sketch, "E14.21.4.4", {"start": v(13.82, -15.2) * mm, "end": v(14.9, -15.2) * mm});
            skArc(sketch, "E14.24.4.4", {"start": v(14.9, -15.2) * mm, "mid": v(15.11, -15.11) * mm, "end": v(15.2, -14.9) * mm});
            skArc(sketch, "E14.28.4.4", {"start": v(15.2, -18.18) * mm, "mid": v(16, -18.32) * mm, "end": v(16.8, -18.18) * mm});
            skArc(sketch, "E14.32.4.4", {"start": v(13.82, -15.2) * mm, "mid": v(13.67, -16) * mm, "end": v(13.82, -16.8) * mm});
            skPoint(sketch, "E14.36.4.4", {"position": v(16, -16) * mm});
            skLineSegment(sketch, "E14.37.4.4", {"start": v(15.2, -18.18) * mm, "end": v(15.2, -17.1) * mm});
            skArc(sketch, "E14.40.4.4", {"start": v(18.18, -16.8) * mm, "mid": v(18.32, -16) * mm, "end": v(18.18, -15.2) * mm});
            skLineSegment(sketch, "E14.44.4.4", {"start": v(16.8, -17.1) * mm, "end": v(16.8, -18.18) * mm});
            skLineSegment(sketch, "E14.47.4.4", {"start": v(16.8, -13.82) * mm, "end": v(16.8, -14.9) * mm});
            skLineSegment(sketch, "E14.50.4.4", {"start": v(17.1, -15.2) * mm, "end": v(18.18, -15.2) * mm});
            skArc(sketch, "E14.53.4.4", {"start": v(16.8, -14.9) * mm, "mid": v(16.89, -15.11) * mm, "end": v(17.1, -15.2) * mm});
            skSolve(sketch);
        }
        {
            var Q0;
            Q0=makeQuery(id+"F0.imprint","IMPRINT",FACE,{"disambiguationData":[TD([[makeQuery(id+"F0.imprint","IMPRINT",EDGE,{"derivedFrom":sQuery(id+"F0.wireOp",EDGE,"E13.0.3.1")}),1.0]])]});
            var Q1;
            Q1=makeQuery(id+"F0.imprint","IMPRINT",FACE,{"disambiguationData":[TD([[makeQuery(id+"F0.imprint","IMPRINT",EDGE,{"derivedFrom":sQuery(id+"F0.wireOp",EDGE,"E13.0.3.2")}),1.0]])]});
            var Q2;
            Q2=makeQuery(id+"F0.imprint","IMPRINT",FACE,{"disambiguationData":[TD([[makeQuery(id+"F0.imprint","IMPRINT",EDGE,{"derivedFrom":sQuery(id+"F0.wireOp",EDGE,"E13.0.3.3")}),1.0]])]});
            var Q3;
            Q3=makeQuery(id+"F0.imprint","IMPRINT",FACE,{"disambiguationData":[TD([[makeQuery(id+"F0.imprint","IMPRINT",EDGE,{"derivedFrom":sQuery(id+"F0.wireOp",EDGE,"71b99deb-29c9-4cb8-8f84-4021775f466b.0.0.5")}),1.0]])]});
            var Q4;
            Q4=makeQuery(id+"F0.imprint","IMPRINT",FACE,{"disambiguationData":[TD([[makeQuery(id+"F0.imprint","IMPRINT",EDGE,{"derivedFrom":sQuery(id+"F0.wireOp",EDGE,"71b99deb-29c9-4cb8-8f84-4021775f466b.0.1.5")}),1.0]])]});
            var Q5;
            Q5=makeQuery(id+"F0.imprint","IMPRINT",FACE,{"disambiguationData":[TD([[makeQuery(id+"F0.imprint","IMPRINT",EDGE,{"derivedFrom":sQuery(id+"F0.wireOp",EDGE,"71b99deb-29c9-4cb8-8f84-4021775f466b.0.2.5")}),1.0]])]});
            var Q6;
            Q6=makeQuery(id+"F0.imprint","IMPRINT",FACE,{"disambiguationData":[TD([[makeQuery(id+"F0.imprint","IMPRINT",EDGE,{"derivedFrom":sQuery(id+"F0.wireOp",EDGE,"71b99deb-29c9-4cb8-8f84-4021775f466b.0.3.5")}),1.0]])]});
            var Q7;
            Q7=makeQuery(id+"F0.imprint","IMPRINT",FACE,{"disambiguationData":[TD([[makeQuery(id+"F0.imprint","IMPRINT",EDGE,{"derivedFrom":sQuery(id+"F0.wireOp",EDGE,"E14.0.4.5")}),1.0]])]});
            var Q8;
            Q8=makeQuery(id+"F0.imprint","IMPRINT",FACE,{"disambiguationData":[TD([[makeQuery(id+"F0.imprint","IMPRINT",EDGE,{"derivedFrom":sQuery(id+"F0.wireOp",EDGE,"E2")}),1.0]])]});
            var Q9;
            Q9=makeQuery(id+"F0.imprint","IMPRINT",FACE,{"disambiguationData":[TD([[makeQuery(id+"F0.imprint","IMPRINT",EDGE,{"derivedFrom":sQuery(id+"F0.wireOp",EDGE,"E11.1.2.0")}),1.0]])]});
            var Q10;
            Q10=makeQuery(id+"F0.imprint","IMPRINT",FACE,{"disambiguationData":[TD([[makeQuery(id+"F0.imprint","IMPRINT",EDGE,{"derivedFrom":sQuery(id+"F0.wireOp",EDGE,"E11.1.3.0")}),1.0]])]});
            var Q11;
            Q11=makeQuery(id+"F0.imprint","IMPRINT",FACE,{"disambiguationData":[TD([[makeQuery(id+"F0.imprint","IMPRINT",EDGE,{"derivedFrom":sQuery(id+"F0.wireOp",EDGE,"E11.1.1.0")}),1.0]])]});
            var Q12;
            Q12=makeQuery(id+"F0.imprint","IMPRINT",FACE,{"disambiguationData":[TD([[makeQuery(id+"F0.imprint","IMPRINT",EDGE,{"derivedFrom":sQuery(id+"F0.wireOp",EDGE,"E11.2.1.0")}),1.0]])]});
            var Q13;
            Q13=makeQuery(id+"F0.imprint","IMPRINT",FACE,{"disambiguationData":[TD([[makeQuery(id+"F0.imprint","IMPRINT",EDGE,{"derivedFrom":sQuery(id+"F0.wireOp",EDGE,"E11.2.2.0")}),1.0]])]});
            var Q14;
            Q14=makeQuery(id+"F0.imprint","IMPRINT",FACE,{"disambiguationData":[TD([[makeQuery(id+"F0.imprint","IMPRINT",EDGE,{"derivedFrom":sQuery(id+"F0.wireOp",EDGE,"E11.2.3.0")}),1.0]])]});
            extrude(context, id + "F1", {"entities" : qUnion([Q0, Q1, Q2, Q3, Q4, Q5, Q6, Q7, Q8, Q9, Q10, Q11, Q12, Q13, Q14]), "depth" : 6 * mm});
        }
        {
            var Q0;
            Q0=qCreatedBy(makeId("Top.planeOp"),FACE);
            var sketch = newSketch(context, id + "F2", { "sketchPlane" : qUnion([Q0])});
            skCircle(sketch, "E15", {"center": v(0, 0) * mm, "radius": 12 * mm});
            skSolve(sketch);
        }
        {
            var Q0;
            Q0=makeQuery(id+"F0.imprint","IMPRINT",FACE,{"disambiguationData":[TD([[makeQuery(id+"F0.imprint","IMPRINT",EDGE,{"derivedFrom":sQuery(id+"F0.wireOp",EDGE,"E2")}),1.0]])]});
            var sketch = newSketch(context, id + "F3", { "sketchPlane" : qUnion([Q0])});
            skLineSegment(sketch, "E16", {"start": v(-2.5, -12) * mm, "end": v(-2.5, -19) * mm});
            skLineSegment(sketch, "E17", {"start": v(2.5, -12) * mm, "end": v(2.5, -19) * mm});
            skLineSegment(sketch, "E18", {"start": v(-2.5, -19) * mm, "end": v(2.5, -19) * mm});
            skLineSegment(sketch, "E19", {"start": v(-2.5, -12) * mm, "end": v(2.5, -12) * mm, "construction": true});
            skArc(sketch, "E20", {"start": v(2.5, -12) * mm, "mid": v(0, 12.25) * mm, "end": v(-2.5, -12) * mm});
            skLineSegment(sketch, "E21.bottom", {"start": v(-19.93, -19.92) * mm, "end": v(19.92, -19.92) * mm});
            skLineSegment(sketch, "E21.top", {"start": v(-19.93, 19.93) * mm, "end": v(19.92, 19.93) * mm});
            skLineSegment(sketch, "E21.left", {"start": v(-19.93, -19.92) * mm, "end": v(-19.93, 19.93) * mm});
            skLineSegment(sketch, "E21.right", {"start": v(19.92, -19.92) * mm, "end": v(19.92, 19.93) * mm});
            skSolve(sketch);
        }
        {
            var Q0;
            Q0 = qSketchRegion(id + "F3", true);
            extrude(context, id + "F4", {"entities" : qUnion([Q0]), "operationType" : NewBodyOperationType.REMOVE, "depth" : 3 * mm});
        }
    });
